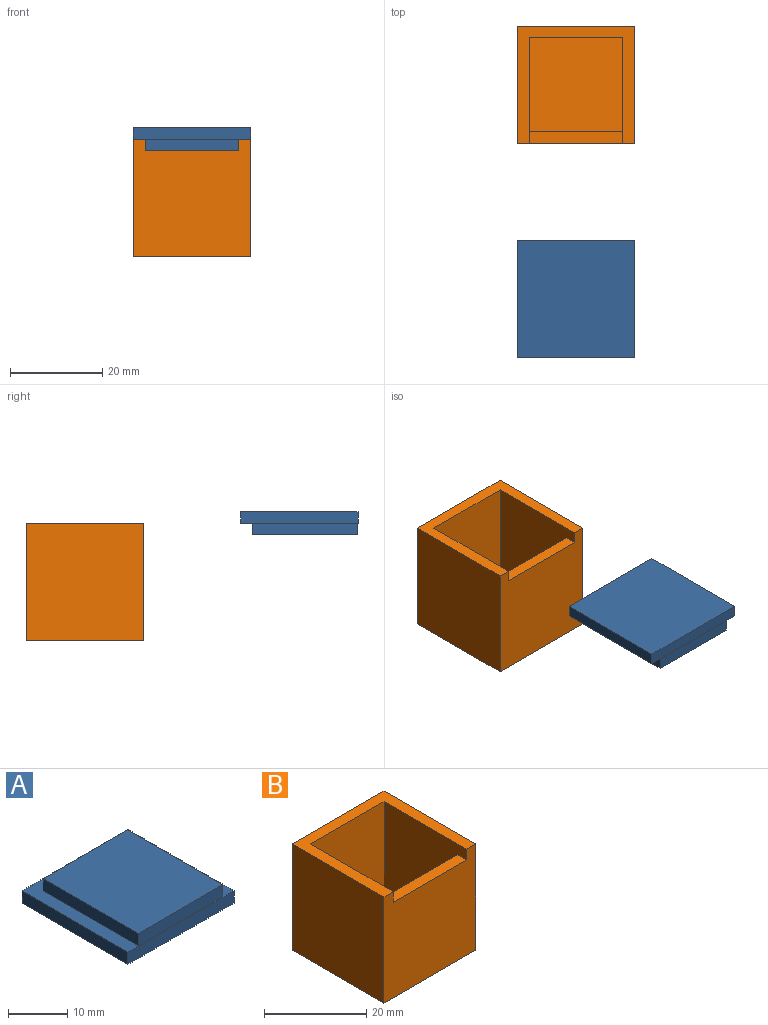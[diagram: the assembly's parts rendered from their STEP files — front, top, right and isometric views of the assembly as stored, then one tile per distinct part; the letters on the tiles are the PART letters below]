
ASSEMBLY  parts=2 mates=1
PART A: 11 faces, bbox 25.4x25.4x5.1 mm
  f0: plane 25.4x2.54mm, normal (-1,0,0), area 64.5mm2, adj f1,f3,f4,f5
  f1: plane 25.4x2.54mm, normal (0,-1,0), area 64.5mm2, adj f0,f2,f4,f5
  f2: plane 25.4x2.54mm, normal (1,0,0), area 64.5mm2, adj f1,f3,f4,f5
  f3: plane 25.4x2.54mm, normal (0,1,0), area 64.5mm2, adj f0,f2,f4,f5
  f4: plane 25.4x25.4mm, normal (0,0,1), area 182.4mm2, adj f0,f1,f2,f3,f6,f7,f8,f9
  f5: plane 25.4x25.4mm, normal (0,0,-1), area 645.2mm2, adj f0,f1,f2,f3
  f6: plane 22.77x2.54mm, normal (-1,0,0), area 57.8mm2, adj f4,f7,f9,f10
  f7: plane 20.32x2.54mm, normal (0,-1,0), area 51.6mm2, adj f4,f6,f8,f10
  f8: plane 22.77x2.54mm, normal (1,0,0), area 57.8mm2, adj f4,f7,f9,f10
  f9: plane 20.32x2.54mm, normal (0,1,0), area 51.6mm2, adj f4,f6,f8,f10
  f10: plane 22.77x20.32mm, normal (0,0,1), area 462.8mm2, adj f6,f7,f8,f9
PART B: 12 faces, bbox 25.4x25.4x25.4 mm
  f0: plane 20.32x2.54mm, normal (0,0,1), area 51.6mm2, adj f4,f6,f8,f9
  f1: plane 25.4x25.4mm, normal (-1,0,0), area 645.2mm2, adj f2,f4,f5,f11
  f2: plane 25.4x25.4mm, normal (0,0,-1), area 645.2mm2, adj f1,f3,f4,f5
  f3: plane 25.4x25.4mm, normal (1,0,0), area 645.2mm2, adj f2,f4,f5,f11
  f4: plane 25.4x25.4mm, normal (0,-1,0), area 593.5mm2, adj f0,f1,f2,f3,f6,f8,f11
  f5: plane 25.4x25.4mm, normal (0,1,0), area 645.2mm2, adj f1,f2,f3,f11
  f6: plane 22.86x22.86mm, normal (1,0,0), area 471mm2, adj f0,f4,f7,f9,f10,f11
  f7: plane 20.32x20.32mm, normal (0,0,1), area 412.9mm2, adj f6,f8,f9,f10
  f8: plane 22.86x22.86mm, normal (-1,0,0), area 471mm2, adj f0,f4,f7,f9,f10,f11
  f9: plane 20.32x20.32mm, normal (0,1,0), area 412.9mm2, adj f0,f6,f7,f8
  f10: plane 22.86x20.32mm, normal (0,-1,0), area 464.5mm2, adj f6,f7,f8,f11
  f11: plane 25.4x25.4mm, normal (0,0,1), area 180.6mm2, adj f1,f3,f4,f5,f6,f8,f10
PLACE A rot(axis=(0,1,0),180deg) t=(-27.69,-16.13,30.09)mm
PLACE B t=(-27.69,43.26,13.58)mm
MATE slider A.f9 <-> B.f10  axis (0,1,0) through (-27.69,-5.83,27.55)mm
